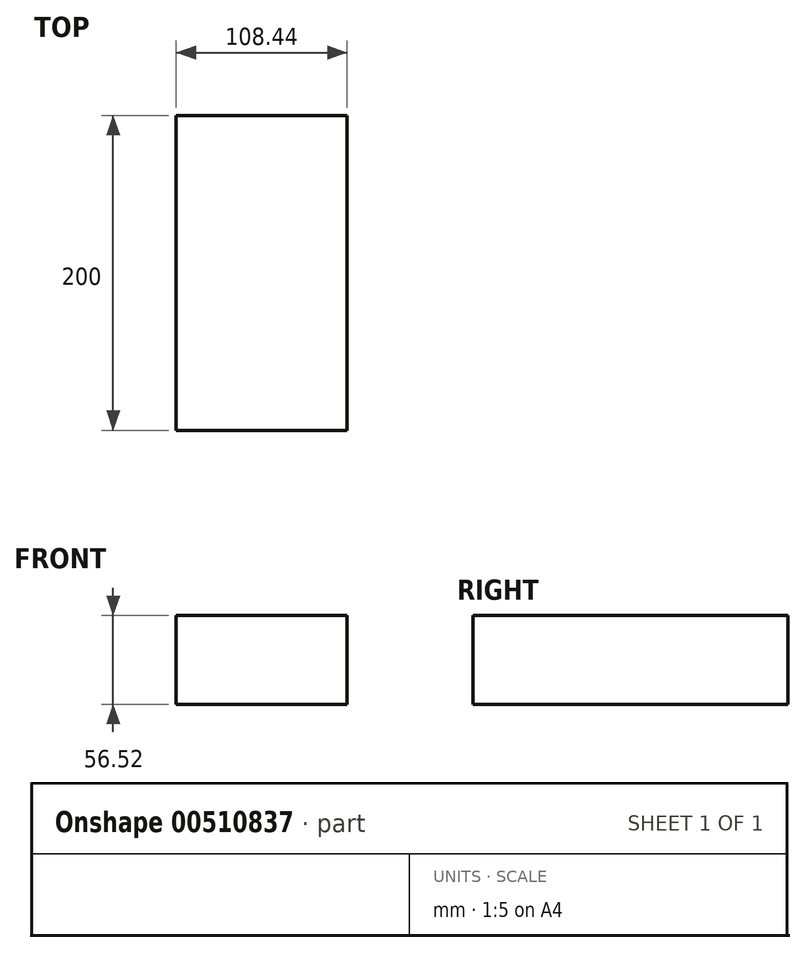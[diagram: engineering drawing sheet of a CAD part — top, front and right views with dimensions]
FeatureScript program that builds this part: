
annotation { "Feature Type Name" : "Feature", "Feature Type Description" : "" }
export const myFeature = defineFeature(function(context is Context, id is Id, definition is map)
    precondition{}
    {
        {
            var Q0;
            Q0=qCreatedBy(makeId("Front.planeOp"),FACE);
            var sketch = newSketch(context, id + "F0", { "sketchPlane" : qUnion([Q0])});
            skLineSegment(sketch, "E0.bottom", {"start": v(-52.21, -28.26) * mm, "end": v(56.23, -28.26) * mm});
            skLineSegment(sketch, "E0.top", {"start": v(-52.21, 28.26) * mm, "end": v(56.23, 28.26) * mm});
            skLineSegment(sketch, "E0.left", {"start": v(-52.21, -28.26) * mm, "end": v(-52.21, 28.26) * mm});
            skLineSegment(sketch, "E0.right", {"start": v(56.23, -28.26) * mm, "end": v(56.23, 28.26) * mm});
            skPoint(sketch, "E0.middle", {"position": v(2, 0) * mm});
            skSolve(sketch);
        }
        {
            var Q0;
            Q0=qSketchRegion(id+"F0",true);
            extrude(context, id + "F1", {"entities" : qUnion([Q0]), "depth" : 200 * mm});
        }
    });
